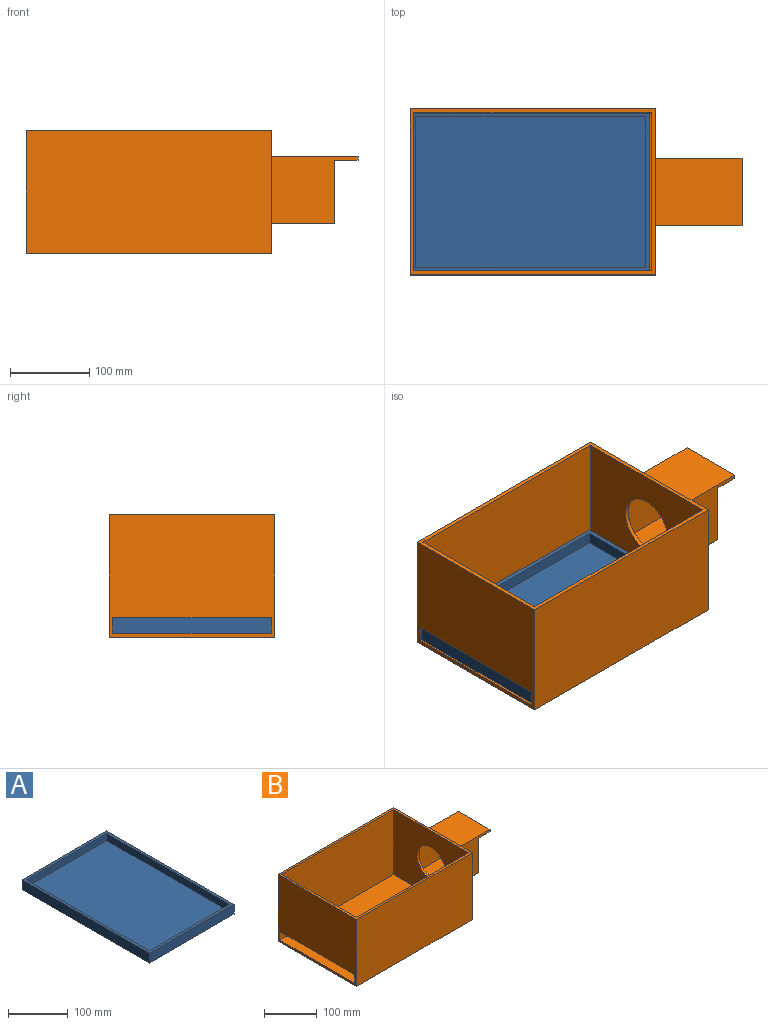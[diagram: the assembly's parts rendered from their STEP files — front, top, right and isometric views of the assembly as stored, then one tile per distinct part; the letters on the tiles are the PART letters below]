
ASSEMBLY  parts=2 mates=1
PART A: 11 faces, bbox 200x300x20 mm
  f0: plane 190x15mm, normal (0,-1,0), area 2850mm2, adj f4,f6,f7,f8
  f1: plane 300x20mm, normal (-1,0,0), area 6000mm2, adj f2,f4,f5,f10
  f2: plane 300x200mm, normal (0,0,-1), area 60000mm2, adj f1,f3,f5,f10
  f3: plane 300x20mm, normal (1,0,0), area 6000mm2, adj f2,f4,f5,f10
  f4: plane 300x200mm, normal (0,0,1), area 4900mm2, adj f0,f1,f3,f5,f6,f8,f9,f10
  f5: plane 200x20mm, normal (0,1,0), area 4000mm2, adj f1,f2,f3,f4
  f6: plane 290x15mm, normal (-1,0,0), area 4350mm2, adj f0,f4,f7,f9
  f7: plane 290x190mm, normal (0,0,1), area 55100mm2, adj f0,f6,f8,f9
  f8: plane 290x15mm, normal (1,0,0), area 4350mm2, adj f0,f4,f7,f9
  f9: plane 190x15mm, normal (0,1,0), area 2850mm2, adj f4,f6,f7,f8
  f10: plane 200x20mm, normal (0,-1,0), area 4000mm2, adj f1,f2,f3,f4
PART B: 27 faces, bbox 420x210x155 mm
  f0: plane 37.5x37.5mm, normal (1,0,0), area 301.8mm2, adj f15,f22,f25
  f1: plane 37.5x37.5mm, normal (1,0,0), area 301.8mm2, adj f15,f17,f25
  f2: plane 210x155mm, normal (1,0,0), area 25325mm2, adj f9,f10,f12,f14,f18,f19,f20,f21
  f3: plane 37.5x37.5mm, normal (1,0,0), area 301.8mm2, adj f15,f17,f23
  f4: plane 37.5x37.5mm, normal (1,0,0), area 301.8mm2, adj f15,f22,f23
  f5: plane 200x130mm, normal (1,0,0), area 26000mm2, adj f9,f11,f13,f16
  f6: plane 210x155mm, normal (-1,0,0), area 28550mm2, adj f8,f9,f10,f11,f12,f13,f14,f16
  f7: plane 200x150mm, normal (-1,0,0), area 25582.1mm2, adj f8,f9,f11,f13,f15
  f8: plane 305x200mm, normal (0,0,1), area 61000mm2, adj f6,f7,f11,f13
  f9: plane 310x210mm, normal (0,0,1), area 5100mm2, adj f2,f5,f6,f7,f11,f12,f13,f14
  f10: plane 310x210mm, normal (0,0,-1), area 65100mm2, adj f2,f6,f12,f14
  f11: plane 305x150mm, normal (0,1,0), area 45100mm2, adj f5,f6,f7,f8,f9,f16
  f12: plane 310x155mm, normal (0,-1,0), area 48050mm2, adj f2,f6,f9,f10
  f13: plane 305x150mm, normal (0,-1,0), area 45100mm2, adj f5,f6,f7,f8,f9,f16
  f14: plane 310x155mm, normal (0,1,0), area 48050mm2, adj f2,f6,f9,f10
  f15: cylinder r=37.5mm len=75mm, axis (1,0,0), area 1178.1mm2, adj f0,f1,f3,f4,f7
  f16: plane 200x5mm, normal (0,0,-1), area 1000mm2, adj f5,f6,f11,f13
  f17: plane 80x75mm, normal (0,1,0), area 6000mm2, adj f1,f3,f23,f24,f25
  f18: plane 110x85mm, normal (0,0,1), area 9350mm2, adj f2,f19,f21,f26
  f19: plane 110x85mm, normal (0,-1,0), area 6950mm2, adj f2,f18,f20,f24,f25,f26
  f20: plane 85x80mm, normal (0,0,-1), area 6800mm2, adj f2,f19,f21,f24
  f21: plane 110x85mm, normal (0,1,0), area 6950mm2, adj f2,f18,f20,f24,f25,f26
  f22: plane 80x75mm, normal (0,-1,0), area 6000mm2, adj f0,f4,f23,f24,f25
  f23: plane 80x75mm, normal (0,0,1), area 6000mm2, adj f3,f4,f17,f22,f24
  f24: plane 85x80mm, normal (1,0,0), area 1175mm2, adj f17,f19,f20,f21,f22,f23,f25
  f25: plane 110x85mm, normal (0,0,-1), area 8550mm2, adj f0,f1,f17,f19,f21,f22,f24,f26
  f26: plane 85x5mm, normal (1,0,0), area 425mm2, adj f18,f19,f21,f25
PLACE A rot(axis=(0,0,-1),90deg) t=(-313.96,162.35,-118.17)mm
PLACE B rot(axis=(0.35,-0.07,0.94),0deg) t=(-461.46,162.35,-53.31)mm
MATE slider A.f2 <-> B.f8  axis (0,0,-1) through (-463.96,162.35,-128.17)mm
